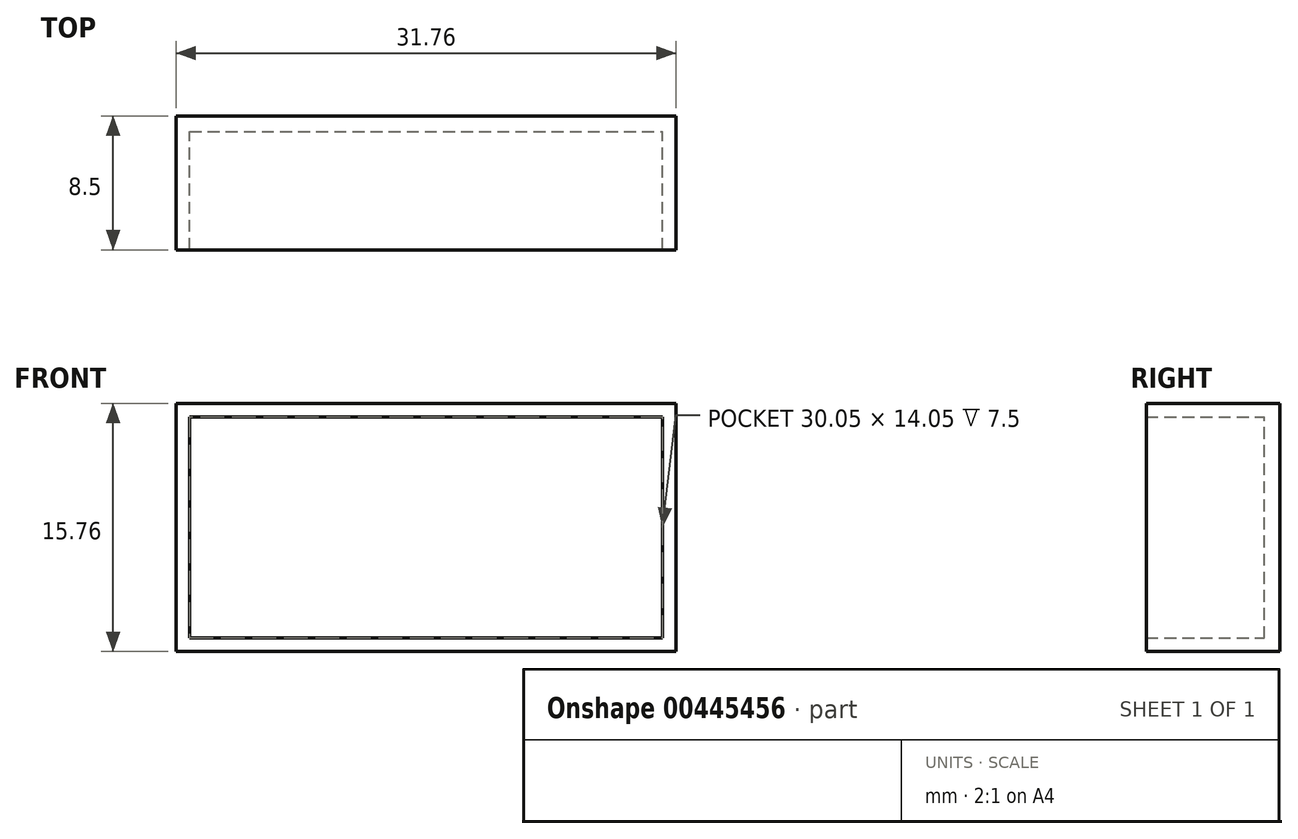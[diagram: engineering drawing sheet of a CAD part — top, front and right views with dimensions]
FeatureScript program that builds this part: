
annotation { "Feature Type Name" : "Feature", "Feature Type Description" : "" }
export const myFeature = defineFeature(function(context is Context, id is Id, definition is map)
    precondition{}
    {
        {
            var Q0;
            Q0=qCreatedBy(makeId("Front.planeOp"),FACE);
            var sketch = newSketch(context, id + "F0", { "sketchPlane" : qUnion([Q0])});
            skLineSegment(sketch, "E0.bottom", {"start": v(15.88, 7.88) * mm, "end": v(-15.88, 7.88) * mm});
            skLineSegment(sketch, "E0.top", {"start": v(15.88, -7.88) * mm, "end": v(-15.88, -7.88) * mm});
            skLineSegment(sketch, "E0.left", {"start": v(15.88, 7.88) * mm, "end": v(15.88, -7.88) * mm});
            skLineSegment(sketch, "E0.right", {"start": v(-15.88, 7.88) * mm, "end": v(-15.88, -7.88) * mm});
            skPoint(sketch, "E0.middle", {"position": v(0, 0) * mm});
            skLineSegment(sketch, "E1.bottom", {"start": v(15.03, 7.03) * mm, "end": v(-15.02, 7.03) * mm});
            skLineSegment(sketch, "E1.top", {"start": v(15.02, -7.03) * mm, "end": v(-15.03, -7.03) * mm});
            skLineSegment(sketch, "E1.left", {"start": v(15.02, 7.03) * mm, "end": v(15.02, -7.03) * mm});
            skLineSegment(sketch, "E1.right", {"start": v(-15.03, 7.03) * mm, "end": v(-15.03, -7.03) * mm});
            skSolve(sketch);
        }
        {
            var Q0;
            Q0=makeQuery(id+"F0.imprint","IMPRINT",FACE,{"disambiguationData":[TD([[makeQuery(id+"F0.imprint","IMPRINT",EDGE,{"derivedFrom":sQuery(id+"F0.wireOp",EDGE,"E1.bottom")}),1.0]])]});
            var Q1;
            Q1=makeQuery(id+"F0.imprint","IMPRINT",FACE,{"disambiguationData":[TD([[makeQuery(id+"F0.imprint","IMPRINT",EDGE,{"derivedFrom":sQuery(id+"F0.wireOp",EDGE,"E0.bottom")}),1.0]])]});
            extrude(context, id + "F1", {"entities" : qUnion([Q0, Q1]), "depth" : 1 * mm});
        }
        {
            var Q0;
            Q0=makeQuery(id+"F0.imprint","IMPRINT",FACE,{"disambiguationData":[TD([[makeQuery(id+"F0.imprint","IMPRINT",EDGE,{"derivedFrom":sQuery(id+"F0.wireOp",EDGE,"E0.bottom")}),1.0]])]});
            extrude(context, id + "F2", {"entities" : qUnion([Q0]), "operationType" : NewBodyOperationType.ADD, "depth" : 8.5 * mm});
        }
    });
